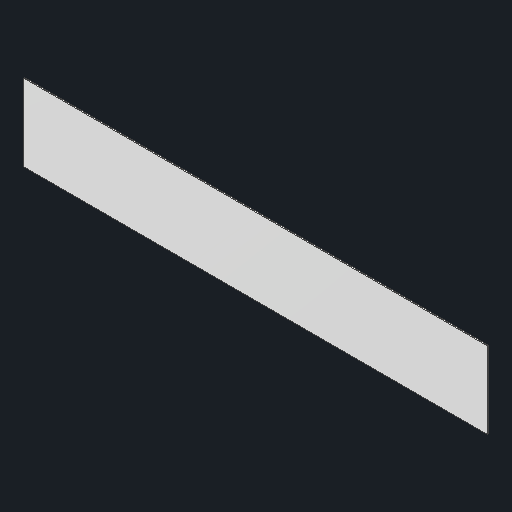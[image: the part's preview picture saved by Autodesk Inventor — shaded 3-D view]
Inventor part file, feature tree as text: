
AUTODESK INVENTOR PART (.ipt)
format: ipt  version: 2025 (Build 290162000, 162)  size: 79,872 bytes
history: native  units: in
note: dims shown in document units (in); Inventor stores cm internally (conversion verified against a paired STEP export)
features: extrude x1
ambient origin geometry x8: Origin, YZ Plane, XZ Plane, XY Plane, X Axis, Y Axis, Z Axis, Center Point
bodies: Solid1 (feature_tree)
feature tree (1):
  extrude  "Extrude1"  [1 undecoded]
note: 1 required parameter value undecoded (feature->parameter linkage not recoverable at this tier; creation-order binding heuristic only, values carry confidence <= 0.55)
